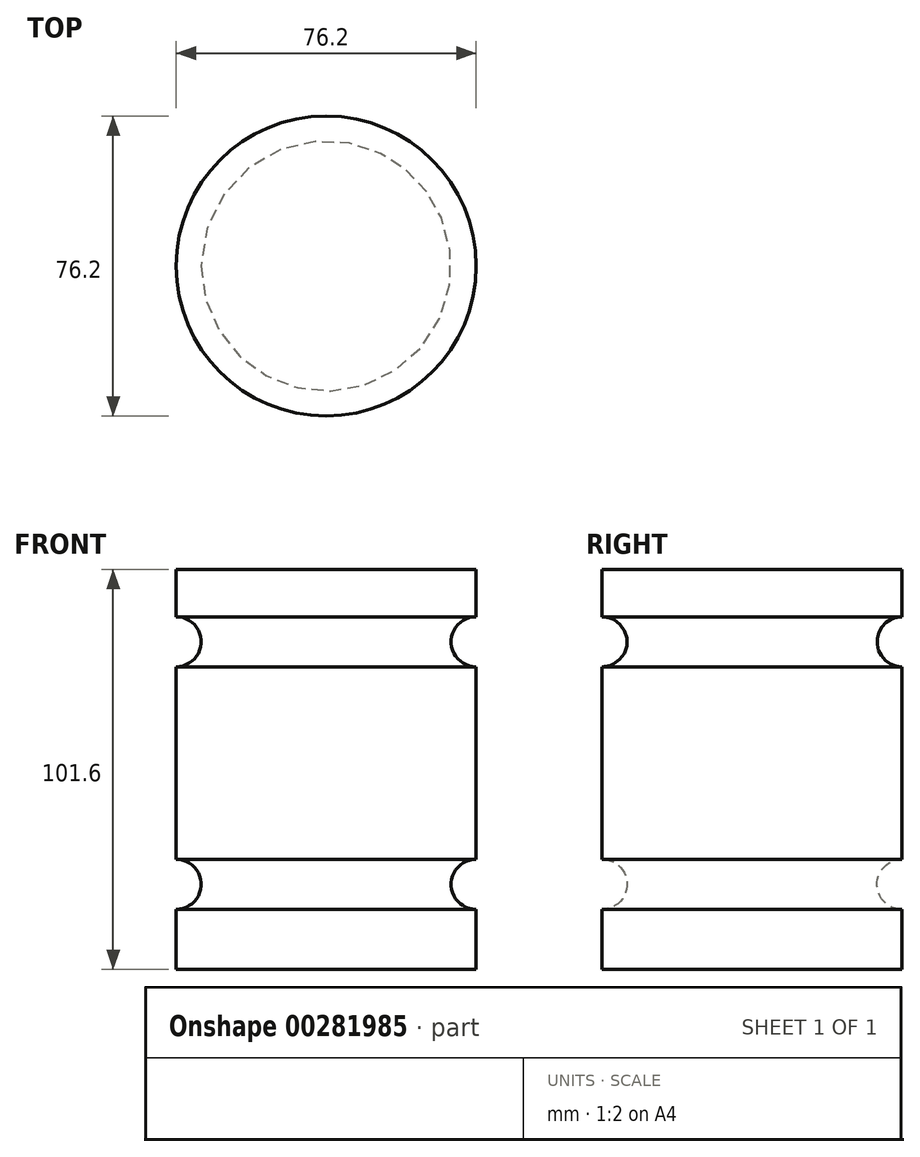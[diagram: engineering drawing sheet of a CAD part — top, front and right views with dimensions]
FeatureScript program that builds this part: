
annotation { "Feature Type Name" : "Feature", "Feature Type Description" : "" }
export const myFeature = defineFeature(function(context is Context, id is Id, definition is map)
    precondition{}
    {
        {
            var Q0;
            Q0=qCreatedBy(makeId("Front.planeOp"),FACE);
            var sketch = newSketch(context, id + "F0", { "sketchPlane" : qUnion([Q0])});
            skLineSegment(sketch, "E0.bottom", {"start": v(0, 0) * mm, "end": v(-38.1, 0) * mm});
            skLineSegment(sketch, "E0.top", {"start": v(0, 101.6) * mm, "end": v(-38.1, 101.6) * mm});
            skLineSegment(sketch, "E0.left", {"start": v(0, 0) * mm, "end": v(0, 15.28) * mm});
            skLineSegment(sketch, "E0.right", {"start": v(-38.1, 0) * mm, "end": v(-38.1, 101.6) * mm});
            skArc(sketch, "E1", {"start": v(0, 89.6) * mm, "mid": v(-6.35, 83.25) * mm, "end": v(0, 76.9) * mm});
            skArc(sketch, "E2", {"start": v(0, 27.98) * mm, "mid": v(-6.35, 21.63) * mm, "end": v(0, 15.28) * mm});
            skLineSegment(sketch, "E3.trimOffspring", {"start": v(0, 89.6) * mm, "end": v(0, 101.6) * mm});
            skLineSegment(sketch, "E4.trimOffspring", {"start": v(0, 27.98) * mm, "end": v(0, 76.9) * mm});
            skSolve(sketch);
        }
        {
            var Q0;
            Q0 = qSketchRegion(id + "F0", true);
            var Q1;
            Q1=sQuery(id+"F0.wireOp",EDGE,"E0.right");
            revolve(context, id + "F1", {"entities" : qUnion([Q0]), "axis" : qUnion([Q1]), "revolveType" : RevolveType.FULL});
        }
    });
